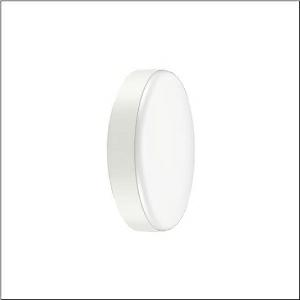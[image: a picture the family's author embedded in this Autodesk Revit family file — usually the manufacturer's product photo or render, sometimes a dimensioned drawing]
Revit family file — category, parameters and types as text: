
# Revit family: round_31_51wc10mb44a
name_source: partatom
category: Lighting Fixtures
units: mm (PartAtom-declared; Revit-internal decimal feet)

## family parameters
Cut with Voids When Loaded = No
Host = Face
Light Source = No
Part Type = Normal
Room Calculation Point = No
Round Connector Dimension = Use Diameter
Shared = No

## types (1)
- --- (1 x LED, 4400 lm, 34 W, 4000K)
    Apparent Load = 34 VA
    CIE Flux Codes = 44 75 94 94 100
    Color Rendering = 80
    Color Temperature = 4000K
    Default Elevation = 1800 mm
    Description = Round 31, wall and ceiling luminaire, primary optical cover: cover, of PC, opal, light emission: direct distribution, primary light characteristic: symmetric, installation type: surface-mounted, LED, rated luminous flux: 4.400lm, luminous efficacy: 129lm/W, light colour: 840, colour temperature: 4000K, control gear: ON/OFF Multilumen, with terminal, 3-pole, max. 2.5mm², mains connection: 220..240V, AC, 50/60Hz, rated input power: 34W, luminaire housing, of PC, traffic white (RAL 9016), diameter: 480mm, protection rating (complete): IP65, insulation class (complete): insulation class II (safety insulation), certification: CE, impact resistance: IK10, permissible operating ambient temperature: -20..+40°C, permissible storage temperature: -20..+60°C, packaging unit: 1 piece
    Height = 97 mm
    Lamp = 1 x LED
    Lamp Light Flux = 4400 lm
    Lamp Power = 34 W
    Lamp count = 1
    Length = 480 mm
    Luminous efficacy = 129 lm/W
    Manufacturer = Siteco
    ModVariant = No
    Model = 51WC10MB44A
    Mounting Place = Ceiling
    Mounting Type = Surface mounted
    Number of Poles = 1
    OnlyDefault = Yes
    Power Factor = 1
    Product Name = Round 31
    Product group = wall and ceiling luminaire | ceiling mounted
    ProductGroupID = 305
    Protection Class = Protection class II
    Protection Degree = IP 65
    RLX_Detail_Level = 1
    RLX_Emergency_Light_Flux = 0 lm
    RLX_Emergency_Type = 0
    RLX_Emergency_Type_DB = No
    RlxData = <blob elided: 42797 chars, md5=4fdf0d8e>
    Socket = socket
    Standby Power = 0 W
    System Light Flux = 4400 lm
    System Power = 34 W
    Type Comments = factory setting: luminous flux: 100 % | (ON | ON)
    Type Image = l_1007188.jpg
    URL = http://relux.com
    VarID = @adj_172289
    Voltage = 0 V
    Weight = 0.00 kg
    Width = 0 mm  [stored 0 ft]

note: [stored X ft] marks values corroborated as IEEE doubles in the binary element streams (Revit-internal decimal feet)

## geometry (parser evidence)
native form markers: Blend x4, Sweep x13
no freeform markers — native parametric forms only
